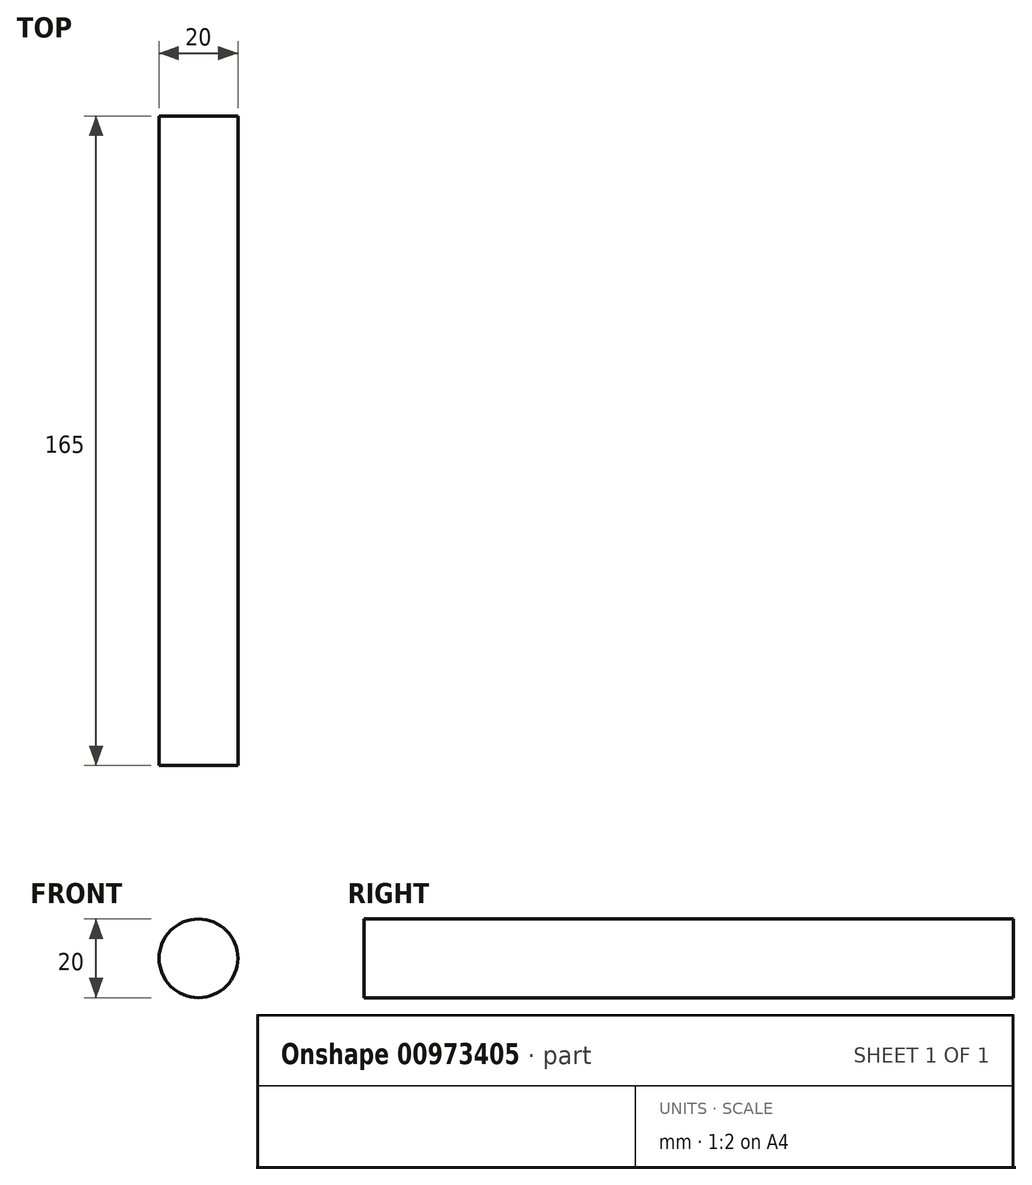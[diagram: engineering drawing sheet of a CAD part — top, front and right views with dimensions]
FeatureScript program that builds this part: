
annotation { "Feature Type Name" : "Feature", "Feature Type Description" : "" }
export const myFeature = defineFeature(function(context is Context, id is Id, definition is map)
    precondition{}
    {
        {
            var Q0;
            Q0=qCreatedBy(makeId("Front.planeOp"),FACE);
            var sketch = newSketch(context, id + "F0", { "sketchPlane" : qUnion([Q0])});
            skCircle(sketch, "E0", {"center": v(0, 0) * mm, "radius": 10 * mm});
            skSolve(sketch);
        }
        {
            var Q0;
            Q0 = qSketchRegion(id + "F0", true);
            extrude(context, id + "F1", {"entities" : qUnion([Q0]), "depth" : 165 * mm, "offsetDistance" : 25 * mm});
        }
    });
